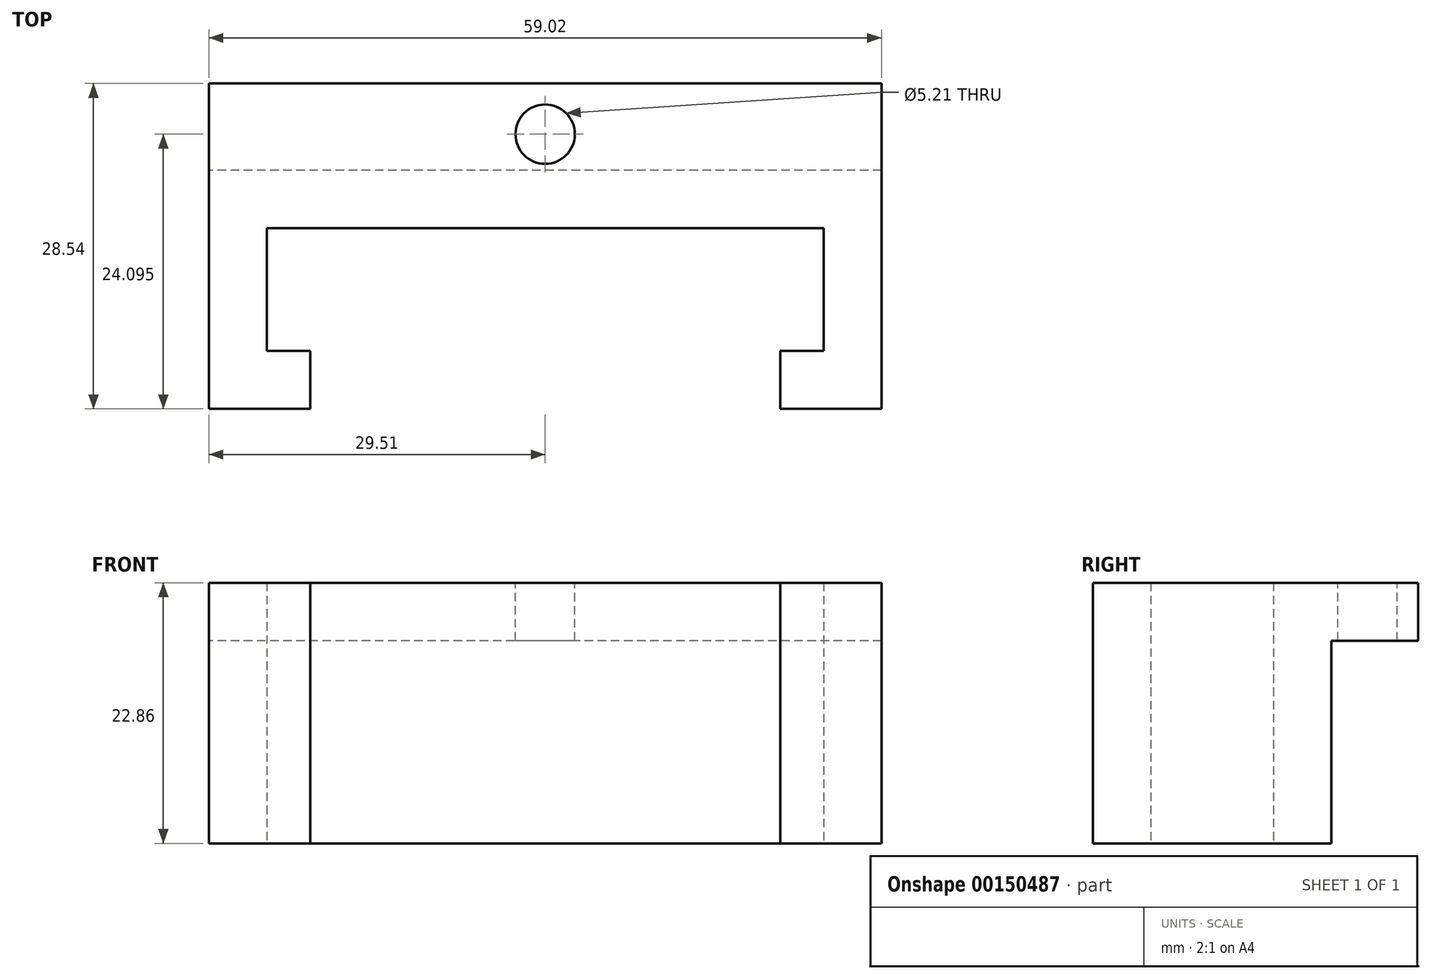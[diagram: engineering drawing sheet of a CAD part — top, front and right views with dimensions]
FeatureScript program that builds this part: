
annotation { "Feature Type Name" : "Feature", "Feature Type Description" : "" }
export const myFeature = defineFeature(function(context is Context, id is Id, definition is map)
    precondition{}
    {
        {
            var Q0;
            Q0=qCreatedBy(makeId("Top.planeOp"),FACE);
            var sketch = newSketch(context, id + "F0", { "sketchPlane" : qUnion([Q0])});
            skLineSegment(sketch, "E0.bottom", {"start": v(24.43, 5.38) * mm, "end": v(-24.43, 5.38) * mm});
            skLineSegment(sketch, "E0.top", {"start": v(24.43, -5.38) * mm, "end": v(-24.43, -5.38) * mm});
            skLineSegment(sketch, "E0.left", {"start": v(24.43, 5.38) * mm, "end": v(24.43, -5.38) * mm});
            skLineSegment(sketch, "E0.right", {"start": v(-24.43, 5.38) * mm, "end": v(-24.43, -5.38) * mm});
            skPoint(sketch, "E0.middle", {"position": v(0, 0) * mm});
            skLineSegment(sketch, "E1.bottom", {"start": v(29.51, 10.46) * mm, "end": v(-29.51, 10.46) * mm});
            skLineSegment(sketch, "E1.top", {"start": v(29.51, -10.46) * mm, "end": v(-29.51, -10.46) * mm});
            skLineSegment(sketch, "E1.left", {"start": v(29.51, 10.46) * mm, "end": v(29.51, -10.46) * mm});
            skLineSegment(sketch, "E1.right", {"start": v(-29.51, 10.46) * mm, "end": v(-29.51, -10.46) * mm});
            skSolve(sketch);
        }
        {
            var Q0;
            Q0=makeQuery(id+"F0.imprint","IMPRINT",FACE,{"disambiguationData":[TD([[makeQuery(id+"F0.imprint","IMPRINT",EDGE,{"derivedFrom":sQuery(id+"F0.wireOp",EDGE,"E0.bottom")}),-1.0]])]});
            extrude(context, id + "F1", {"entities" : qUnion([Q0]), "depth" : 22.86 * mm});
        }
        {
            var Q0;
            Q0=makeQuery(id+"F1.opExtrude","CAP_FACE",FACE,{"disambiguationData":[OSD([sQuery(id+"F0.wireOp",EDGE,"E0.bottom"),sQuery(id+"F0.wireOp",EDGE,"E0.top"),sQuery(id+"F0.wireOp",EDGE,"E0.left"),sQuery(id+"F0.wireOp",EDGE,"E0.right"),sQuery(id+"F0.wireOp",EDGE,"E1.bottom"),sQuery(id+"F0.wireOp",EDGE,"E1.top"),sQuery(id+"F0.wireOp",EDGE,"E1.left"),sQuery(id+"F0.wireOp",EDGE,"E1.right")])],"isStart":false});
            var sketch = newSketch(context, id + "F2", { "sketchPlane" : qUnion([Q0])});
            skLineSegment(sketch, "E2.bottom", {"start": v(-29.51, 10.46) * mm, "end": v(29.51, 10.46) * mm});
            skLineSegment(sketch, "E2.top", {"start": v(-29.51, 18.08) * mm, "end": v(29.51, 18.08) * mm});
            skLineSegment(sketch, "E2.left", {"start": v(-29.51, 10.46) * mm, "end": v(-29.51, 18.08) * mm});
            skLineSegment(sketch, "E2.right", {"start": v(29.51, 10.46) * mm, "end": v(29.51, 18.08) * mm});
            skCircle(sketch, "E3", {"center": v(0, 13.64) * mm, "radius": 2.6 * mm});
            skPoint(sketch, "E3.centerSnap0", {"position": v(0, 10.46) * mm});
            skLineSegment(sketch, "E4", {"start": v(-29.51, 14.27) * mm, "end": v(29.51, 14.27) * mm, "construction": true});
            skSolve(sketch);
        }
        {
            var Q0;
            Q0=makeQuery(id+"F2.imprint","IMPRINT",FACE,{"disambiguationData":[TD([[makeQuery(id+"F2.imprint","IMPRINT",EDGE,{"derivedFrom":sQuery(id+"F2.wireOp",EDGE,"E2.bottom")}),-1.0]])]});
            extrude(context, id + "F3", {"entities" : qUnion([Q0]), "operationType" : NewBodyOperationType.ADD, "oppositeDirection" : true, "depth" : 5.08 * mm});
        }
        {
            var Q0;
            Q0=makeQuery(id+"F1.opExtrude","CAP_FACE",FACE,{"disambiguationData":[OSD([sQuery(id+"F0.wireOp",EDGE,"E0.bottom"),sQuery(id+"F0.wireOp",EDGE,"E0.top"),sQuery(id+"F0.wireOp",EDGE,"E0.left"),sQuery(id+"F0.wireOp",EDGE,"E0.right"),sQuery(id+"F0.wireOp",EDGE,"E1.bottom"),sQuery(id+"F0.wireOp",EDGE,"E1.top"),sQuery(id+"F0.wireOp",EDGE,"E1.left"),sQuery(id+"F0.wireOp",EDGE,"E1.right")])],"isStart":true});
            var sketch = newSketch(context, id + "F4", { "sketchPlane" : qUnion([Q0])});
            skLineSegment(sketch, "E5.bottom", {"start": v(20.62, 5.38) * mm, "end": v(-20.62, 5.38) * mm});
            skLineSegment(sketch, "E5.top", {"start": v(20.62, 10.46) * mm, "end": v(-20.62, 10.46) * mm});
            skLineSegment(sketch, "E5.left", {"start": v(20.62, 5.38) * mm, "end": v(20.62, 10.46) * mm});
            skLineSegment(sketch, "E5.right", {"start": v(-20.62, 5.38) * mm, "end": v(-20.62, 10.46) * mm});
            skSolve(sketch);
        }
        {
            var Q0;
            Q0=makeQuery(id+"F4.imprint","IMPRINT",FACE,{"disambiguationData":[TD([[makeQuery(id+"F4.imprint","IMPRINT",EDGE,{"derivedFrom":sQuery(id+"F4.wireOp",EDGE,"E5.bottom")}),-1.0]])]});
            extrude(context, id + "F5", {"entities" : qUnion([Q0]), "operationType" : NewBodyOperationType.REMOVE, "endBound" : BoundingType.THROUGH_ALL, "oppositeDirection" : true, "depth" : 25.4 * mm});
        }
    });
